# Revit family: 431180001_Griferia Lavamanos Dalia Plus 4 Pulgadas
name_source: partatom
category: Plumbing Fixtures
units: mm (PartAtom-declared; Revit-internal decimal feet)

## family parameters
Cut with Voids When Loaded = No
Host = Face
OmniClass Number = 23.31.11.00
OmniClass Title = Faucets
Part Type = Normal
Room Calculation Point = No
Round Connector Dimension = Use Diameter
Shared = No

## types (1)
- 431180001_Griferia Lavamanos Dalia Plus 4 Pulgadas
    Alto = 129 mm  [stored 0.423228 ft]
    Ancho = 211 mm  [stored 0.692257 ft]
    Capacidad de flujo = 8,3 L/min.
    Creado por = BIMBAU
    Default Elevation = 1219 mm
    Description = Resistente a la corrosión, pelado y decoloración por agua, Recubrimientos no tóxicos, Condición de servicio recomendada, uso doméstico. Genera un chorro de agua espumoso, agradable al tacto y a la vista, ahorra agua. Acabado brillante, brinda la apariencia de material acero.nnGarantía por 45 años
    Fecha de creación = 07/04/2021
    Garantía = 30  Años Grival - 2 Años Cromado
    Manufacturer = Grival
    Material = Corona_Aluminio
    Model = Griferia Dalia Plus Lavamanos 4 Pulgadas
    Peso Bruto aprox = 610gr. / 1,34 lb.
    Peso Neto aprox = 1590gr. / 1,30 lb.
    Presion maxima = 125 psi.
    Presion minima = 20 psi.
    Profundidad = 149 mm  [stored 0.488845 ft]
    Referencia = 431180001
    Temperaturas máxima de trabajo = 71 ºC / 159,8 ºF.
    Temperaturas mínima de trabajo = 5 ºC / 41 ºF
    URL = https://www.grival.com
    Vida útil = 500.000 ciclos.

note: [stored X ft] marks values corroborated as IEEE doubles in the binary element streams (Revit-internal decimal feet)

## geometry (parser evidence)
native form markers: Sweep x3
no freeform markers — native parametric forms only
